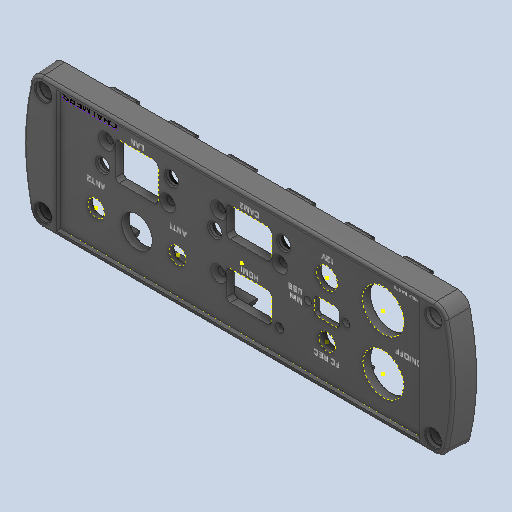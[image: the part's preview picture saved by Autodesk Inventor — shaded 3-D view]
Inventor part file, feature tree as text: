
AUTODESK INVENTOR PART (.ipt)
format: ipt  version: 2024.2 (Build 282272000, 272)  size: 1,269,760 bytes
history: native  units: mm
features: extrude x14, sketch x7, fillet x5, other x4, plane x3, chamfer x2, mirror x1, hole x1, reference x1
ambient origin geometry x8: Origin, YZ Plane, XZ Plane, XY Plane, X Axis, Y Axis, Z Axis, Center Point
bodies: Solid1 (feature_tree)
feature tree (38):
  other  "1009799_3D"
  extrude  "Extrusion1"  Depth=4.85mm
  fillet  "Fillet1"  Radius=27.0mm
  plane  "Work Plane1"
  extrude  "Extrusion2"  Depth=3.5mm
  chamfer  "Chamfer1"  Distance=11.55mm
  plane  "Work Plane3"
  mirror  "Mirror2"
  extrude  "Extrusion7"  Depth=3.5mm
  extrude  "Extrusion8"  TaperAngle=0.0deg  [1 undecoded]
  extrude  "Extrusion9"  Depth=3.5mm
  extrude  "Extrusion10"  Depth=3.5mm
  extrude  "Extrusion11"  Depth=3.5mm
  fillet  "Fillet3"  Radius=1.85mm
  extrude  "Extrusion12"  Depth=1.35mm
  fillet  "Fillet4"  Radius=10.0mm
  extrude  "Extrusion13"  Depth=2.0mm TaperAngle=45.0deg
  extrude  "Extrusion14"  Depth=3.5mm
  hole  "Hole1"  [1 undecoded]
  extrude  "Extrusion16"  Depth=3.5mm
  fillet  "Fillet5"  Radius=3.225mm
  extrude  "Extrusion17"  Depth=3.5mm
  extrude  "Extrusion18"  Depth=3.5mm
  fillet  "Fillet6"  Radius=0.05mm
  extrude  "Extrusion19"  Depth=3.5mm
  chamfer  "Chamfer6"  Distance=11.5mm
  sketch  "Sketch29"  dims[d11=16.55mm d12=11.55mm d14=17.0mm d15=0.0mm d16=0.0mm d17=6.35mm d20=8.225mm d21=6.9mm d22=1.85mm d23=1.35mm d26=-1.5mm d27=10.0mm d28=0.0mm d29=0.5mm d30=2.0mm d31=45.0deg d65=9.408852mm d66=4.85mm d67=4.85mm d68=27.0mm d69=9.0mm d70=3.3mm d71=3.3mm d72=24.0mm d73=17.55mm d74=11.55mm d75=6.35mm d76=1.85mm d77=1.275mm d78=3.725mm d79=3.225mm d80=4.725mm d81=5.225mm d82=0.05mm d83=0.05mm d85=11.5mm d86=4.85mm d87=4.85mm d88=27.0mm d90=3.3mm d91=3.3mm d92=24.0mm d93=16.55mm d94=14.55mm d95=9.0mm d96=4.5mm d97=3.725mm d98=5.225mm d100=0.05mm d101=3.725mm d102=5.225mm d104=7.0mm d105=7.0mm d106=7.0mm d107=7.0mm d108=4.5mm d109=4.5mm d112=9.125mm d113=9.125mm d114=30.0mm d115=44.0mm d116=10.0mm d117=0.0mm d118=11.55mm d119=5.775mm d120=16.0mm d121=16.0mm d122=6.5mm d123=6.5mm d124=12.2mm d125=16.0mm d126=16.0mm d128=16.55mm d129=21.725mm d130=30.0mm d132=10.075mm d134=16.2mm d135=8.13mm d136=0.0mm d137=22.0mm d138=0.0mm d139=0.0mm d141=6.35mm d142=0.0mm d143=0.0mm d144=10.0mm d145=0.0mm d147=1.275mm d148=1.275mm d149=13.908852mm d150=0.7125mm d151=11.55mm d152=5.775mm d154=11.55mm d155=9.75mm d156=6.75mm d157=3.0mm d158=7.5mm d159=0.0mm d160=0.0mm d161=1.25mm d164=16.0mm d165=4.875mm d166=9.75mm d167=22.0mm d168=11.0mm d169=1.5mm d170=0.0mm d171=2.0mm d172=12.4mm d173=0.0mm d174=0.0mm d175=1.5mm d176=0.0mm d177=6.5mm d178=0.0mm d179=0.0mm d199=3.25mm d200=6.0mm d201=6.25mm d202=2.0mm d203=90.0deg d204=8.0mm d205=20.594885mm d206=13.0mm d207=10.0mm d208=0.0mm d209=2.0mm d210=14.0mm d211=14.0mm d212=1.5mm d213=0.0mm d214=20.0mm d215=0.2mm d216=0.0mm d217=0.0mm d218=3.0mm d219=20.0mm d220=0.0mm d221=7.877954mm d222=0.2mm d223=2.0mm d224=45.0deg d225=1.5mm d226=0.8mm d227=0.8mm d228=1.5mm d229=0.85mm d230=6.75mm d231=4.75mm d232=5.0mm d233=2.75mm d234=3.5mm d235=1.5mm d236=5.0mm d237=1.0mm d238=1.0mm d239=4.75mm d240=1.0mm d241=5.5mm d242=4.5mm d243=4.5mm d244=3.5mm d245=3.5mm]
  plane  "Work Plane2"
  sketch  "Sketch11"  dims[d0=4.85mm d1=4.85mm d2=27.0mm]
  sketch  "Sketch12"  dims[d3=9.0mm d4=3.5mm]
  sketch  "Sketch14"  dims[d6=3.3mm]
  sketch  "Sketch15"  dims[d7=3.3mm]
  sketch  "Sketch16"  dims[d8=24.0mm]
  sketch  "Sketch17"  dims[d9=5.0mm]
  reference  "Reference1"
  other  "Image1"
  other  "<userpath>\Google Drive\Unicorn 2020\CAD\Assembly.iam"
  other  "Assembly.iam"
note: 2 required parameter values undecoded (feature->parameter linkage not recoverable at this tier; creation-order binding heuristic only, values carry confidence <= 0.55)
